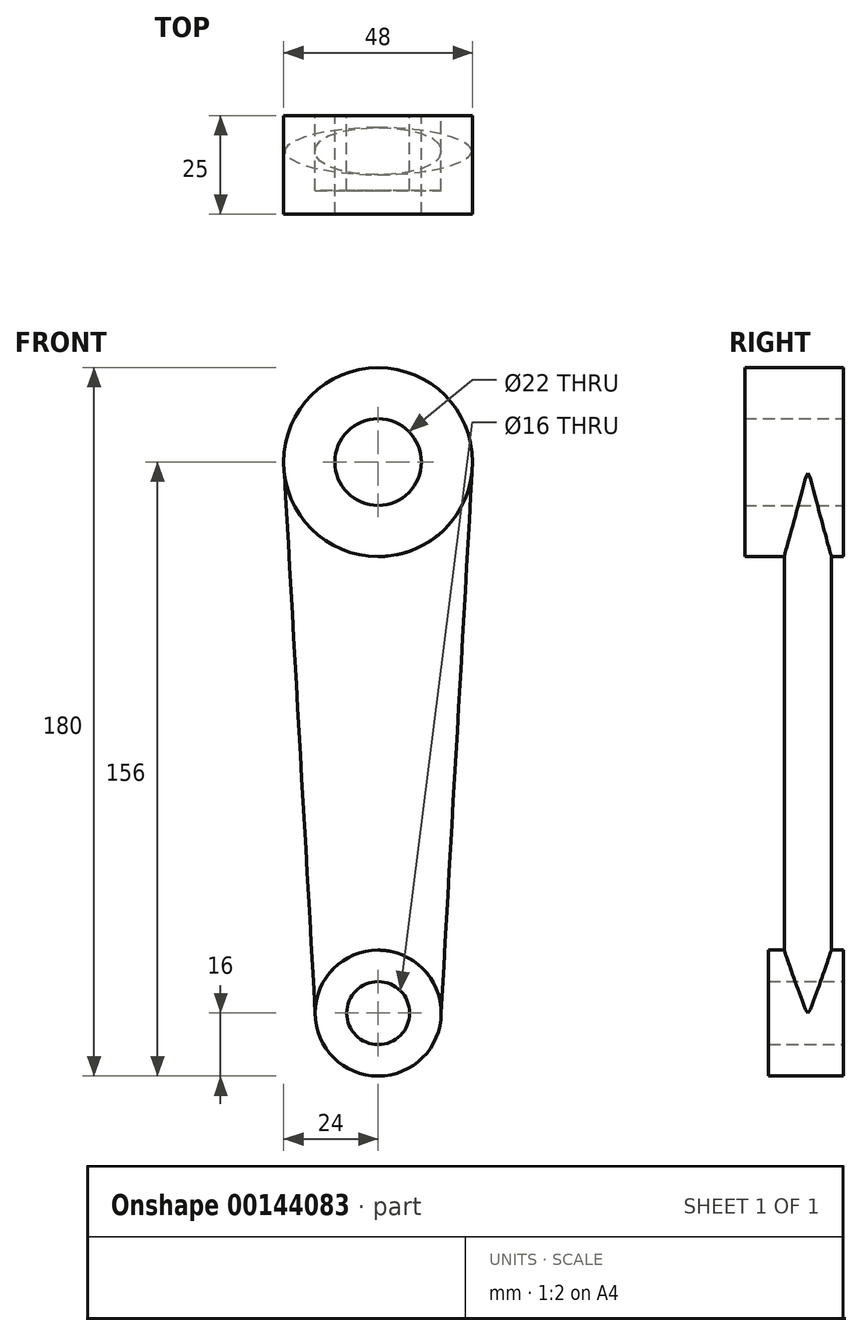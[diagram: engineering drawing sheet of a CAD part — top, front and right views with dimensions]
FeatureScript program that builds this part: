
annotation { "Feature Type Name" : "Feature", "Feature Type Description" : "" }
export const myFeature = defineFeature(function(context is Context, id is Id, definition is map)
    precondition{}
    {
        {
            var Q0;
            Q0=qCreatedBy(makeId("Front.planeOp"),FACE);
            var sketch = newSketch(context, id + "F0", { "sketchPlane" : qUnion([Q0])});
            skCircle(sketch, "E0", {"center": v(0, 0) * mm, "radius": 8 * mm});
            skCircle(sketch, "E1", {"center": v(0, 0) * mm, "radius": 16 * mm});
            skCircle(sketch, "E2", {"center": v(0, 140) * mm, "radius": 11 * mm});
            skCircle(sketch, "E3", {"center": v(0, 140) * mm, "radius": 24 * mm});
            skSolve(sketch);
        }
        {
            var Q0;
            Q0=makeQuery(id+"F0.imprint","IMPRINT",FACE,{"disambiguationData":[TD([[makeQuery(id+"F0.imprint","IMPRINT",EDGE,{"derivedFrom":sQuery(id+"F0.wireOp",EDGE,"E0")}),-1.0]])]});
            var Q1;
            Q1=makeQuery(id+"F0.imprint","IMPRINT",FACE,{"disambiguationData":[TD([[makeQuery(id+"F0.imprint","IMPRINT",EDGE,{"derivedFrom":sQuery(id+"F0.wireOp",EDGE,"E0")}),1.0]])]});
            extrude(context, id + "F1", {"entities" : qUnion([Q0, Q1]), "depth" : 19 * mm});
        }
        {
            var Q0;
            Q0=makeQuery(id+"F0.imprint","IMPRINT",FACE,{"disambiguationData":[TD([[makeQuery(id+"F0.imprint","IMPRINT",EDGE,{"derivedFrom":sQuery(id+"F0.wireOp",EDGE,"E2")}),-1.0]])]});
            var Q1;
            Q1=makeQuery(id+"F0.imprint","IMPRINT",FACE,{"disambiguationData":[TD([[makeQuery(id+"F0.imprint","IMPRINT",EDGE,{"derivedFrom":sQuery(id+"F0.wireOp",EDGE,"E2")}),1.0]])]});
            extrude(context, id + "F2", {"entities" : qUnion([Q0, Q1]), "depth" : 25 * mm});
        }
        {
            var Q0;
            Q0=qCreatedBy(makeId("Top.planeOp"),FACE);
            var sketch = newSketch(context, id + "F3", { "sketchPlane" : qUnion([Q0])});
            skEllipse(sketch, "E4", {"center": v(0, -9) * mm, "majorRadius": 16 * mm, "minorRadius": 6 * mm, "majorAxis": v(1, 0)});
            skPoint(sketch, "E5", {"position": v(0, -3) * mm});
            skLineSegment(sketch, "E6", {"start": v(16, 0) * mm, "end": v(16, -19) * mm, "construction": true});
            skSolve(sketch);
        }
        {
            var Q0;
            Q0=sQuery(id+"F0.wireOp",VERTEX,"E3.center");
            var Q1;
            Q1=qCreatedBy(makeId("Top.planeOp"),FACE);
            cPlane(context, id + "F4", {"entities" : qUnion([Q0, Q1]), "cplaneType" : CPlaneType.PLANE_POINT, "offset" : 25 * mm, "width" : 150 * mm, "height" : 150 * mm});
        }
        {
            var Q0;
            Q0=qCreatedBy(id+"F4.planeOp",FACE);
            var sketch = newSketch(context, id + "F5", { "sketchPlane" : qUnion([Q0])});
            skEllipse(sketch, "E7", {"center": v(0, -9) * mm, "majorRadius": 24 * mm, "minorRadius": 6 * mm, "majorAxis": v(1, 0)});
            skLineSegment(sketch, "E8", {"start": v(24, 0) * mm, "end": v(24, -25) * mm, "construction": true});
            skSolve(sketch);
        }
        {
            var Q0;
            Q0=makeQuery(id+"F5.imprint","IMPRINT",FACE,{"disambiguationData":[TD([[makeQuery(id+"F5.imprint","IMPRINT",EDGE,{"derivedFrom":sQuery(id+"F5.wireOp",EDGE,"E7")}),1.0]])]});
            var Q1;
            Q1=makeQuery(id+"F3.imprint","IMPRINT",FACE,{"disambiguationData":[TD([[makeQuery(id+"F3.imprint","IMPRINT",EDGE,{"derivedFrom":sQuery(id+"F3.wireOp",EDGE,"E4")}),1.0]])]});
            loft(context, id + "F6", {"operationType" : NewBodyOperationType.ADD, "sheetProfilesArray" : [{ "sheetProfileEntities" : qUnion([Q0]) }, { "sheetProfileEntities" : qUnion([Q1]) }]});
        }
        {
            var Q0;
            Q0=makeQuery(id+"F0.imprint","IMPRINT",FACE,{"disambiguationData":[TD([[makeQuery(id+"F0.imprint","IMPRINT",EDGE,{"derivedFrom":sQuery(id+"F0.wireOp",EDGE,"E2")}),1.0]])]});
            extrude(context, id + "F7", {"entities" : qUnion([Q0]), "operationType" : NewBodyOperationType.REMOVE, "endBound" : BoundingType.THROUGH_ALL, "depth" : 25 * mm});
        }
        {
            var Q0;
            Q0=makeQuery(id+"F0.imprint","IMPRINT",FACE,{"disambiguationData":[TD([[makeQuery(id+"F0.imprint","IMPRINT",EDGE,{"derivedFrom":sQuery(id+"F0.wireOp",EDGE,"E0")}),1.0]])]});
            extrude(context, id + "F8", {"entities" : qUnion([Q0]), "operationType" : NewBodyOperationType.REMOVE, "endBound" : BoundingType.THROUGH_ALL, "depth" : 25 * mm});
        }
    });
